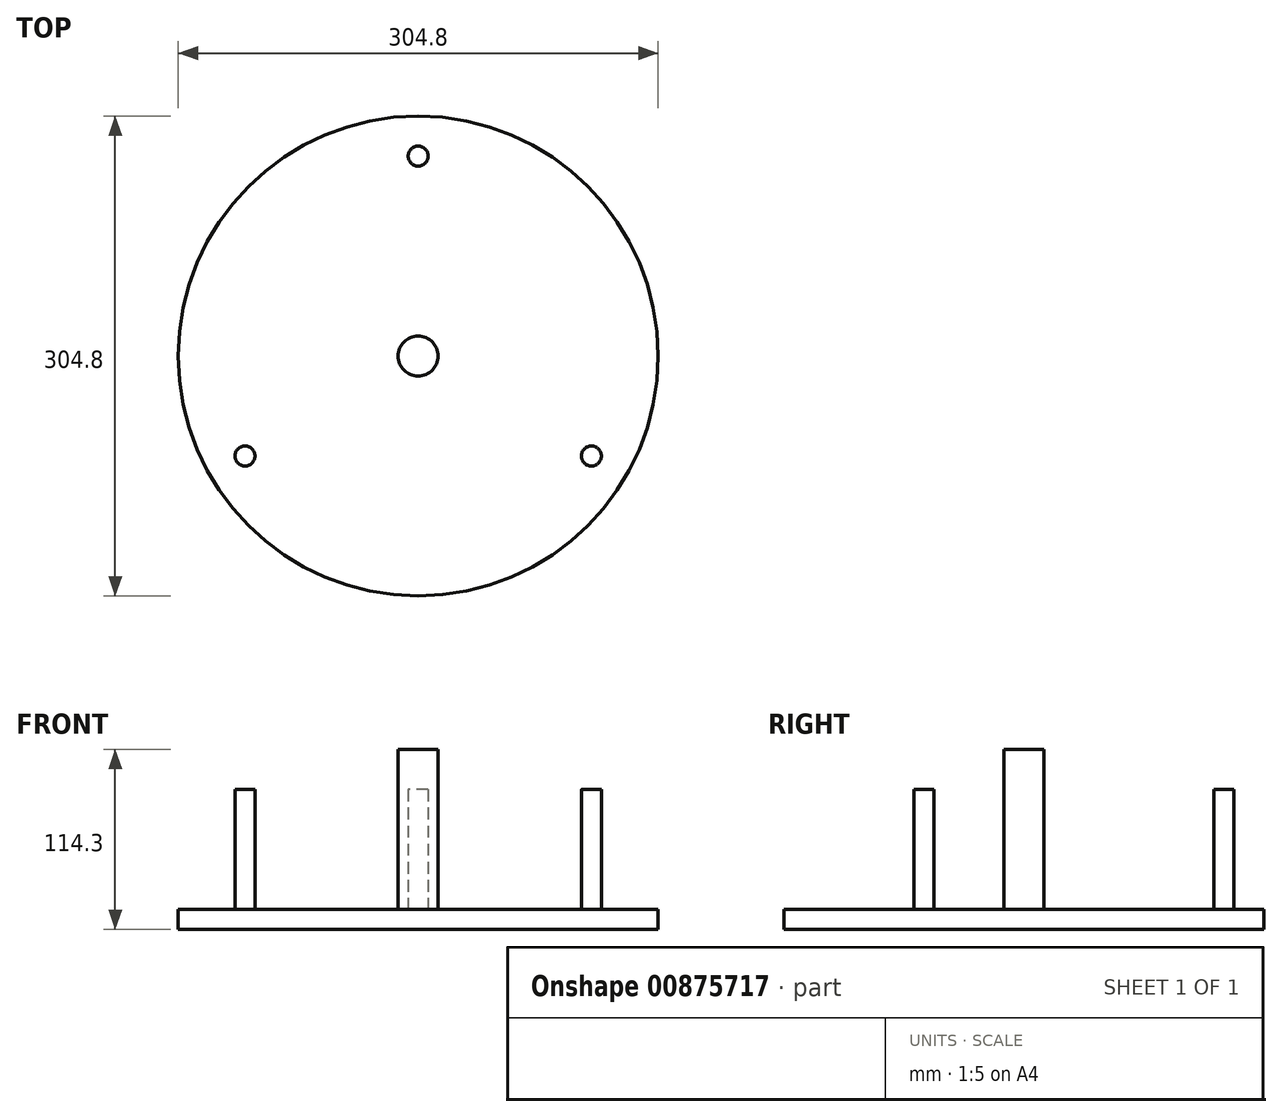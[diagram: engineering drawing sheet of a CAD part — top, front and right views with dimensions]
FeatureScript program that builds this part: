
annotation { "Feature Type Name" : "Feature", "Feature Type Description" : "" }
export const myFeature = defineFeature(function(context is Context, id is Id, definition is map)
    precondition{}
    {
        {
            var Q0;
            Q0=qCreatedBy(makeId("Top.planeOp"),FACE);
            var sketch = newSketch(context, id + "F0", { "sketchPlane" : qUnion([Q0])});
            skCircle(sketch, "E0", {"center": v(0, 0) * mm, "radius": 152.4 * mm});
            skSolve(sketch);
        }
        {
            var Q0;
            Q0=makeQuery(id+"F0.imprint","IMPRINT",FACE,{"disambiguationData":[TD([[makeQuery(id+"F0.imprint","IMPRINT",EDGE,{"derivedFrom":sQuery(id+"F0.wireOp",EDGE,"E0")}),1.0]])]});
            extrude(context, id + "F1", {"entities" : qUnion([Q0]), "depth" : 12.7 * mm, "offsetDistance" : 25.4 * mm});
        }
        {
            var Q0;
            Q0=makeQuery(id+"F1.opExtrude","CAP_FACE",FACE,{"disambiguationData":[OSD([sQuery(id+"F0.wireOp",EDGE,"E0")])],"isStart":false});
            var sketch = newSketch(context, id + "F2", { "sketchPlane" : qUnion([Q0])});
            skCircle(sketch, "E1", {"center": v(0, 0) * mm, "radius": 12.7 * mm});
            skSolve(sketch);
        }
        {
            var Q0;
            Q0=makeQuery(id+"F2.imprint","IMPRINT",FACE,{"disambiguationData":[TD([[makeQuery(id+"F2.imprint","IMPRINT",EDGE,{"derivedFrom":sQuery(id+"F2.wireOp",EDGE,"E1")}),1.0]])]});
            extrude(context, id + "F3", {"entities" : qUnion([Q0]), "operationType" : NewBodyOperationType.ADD, "depth" : 101.6 * mm, "offsetDistance" : 25.4 * mm});
        }
        {
            var Q0;
            Q0=makeQuery(id+"F1.opExtrude","CAP_FACE",FACE,{"disambiguationData":[OSD([sQuery(id+"F0.wireOp",EDGE,"E0")])],"isStart":false});
            var sketch = newSketch(context, id + "F4", { "sketchPlane" : qUnion([Q0])});
            skCircle(sketch, "E2", {"center": v(0, 127) * mm, "radius": 6.35 * mm});
            skSolve(sketch);
        }
        {
            var Q0;
            Q0=makeQuery(id+"F4.imprint","IMPRINT",FACE,{"disambiguationData":[TD([[makeQuery(id+"F4.imprint","IMPRINT",EDGE,{"derivedFrom":sQuery(id+"F4.wireOp",EDGE,"E2")}),1.0]])]});
            extrude(context, id + "F5", {"entities" : qUnion([Q0]), "operationType" : NewBodyOperationType.ADD, "depth" : 76.2 * mm, "offsetDistance" : 25.4 * mm});
        }
        {
            var Q0;
            Q0=makeQuery(id+"F1.opExtrude","SWEPT_BODY",BODY,{"disambiguationData":[OSD([sQuery(id+"F0.wireOp",EDGE,"E0")])]});
            var Q1;
            Q1=makeQuery(id+"F3.opExtrude","SWEPT_FACE",FACE,{"disambiguationData":[OSD([sQuery(id+"F2.wireOp",EDGE,"E1")])]});
            circularPattern(context, id + "F6", {"operationType" : NewBodyOperationType.ADD, "entities" : qUnion([Q0]), "axis" : qUnion([Q1]), "angle" : 360 * degree, "instanceCount" : 3, "equalSpace" : true});
        }
    });
